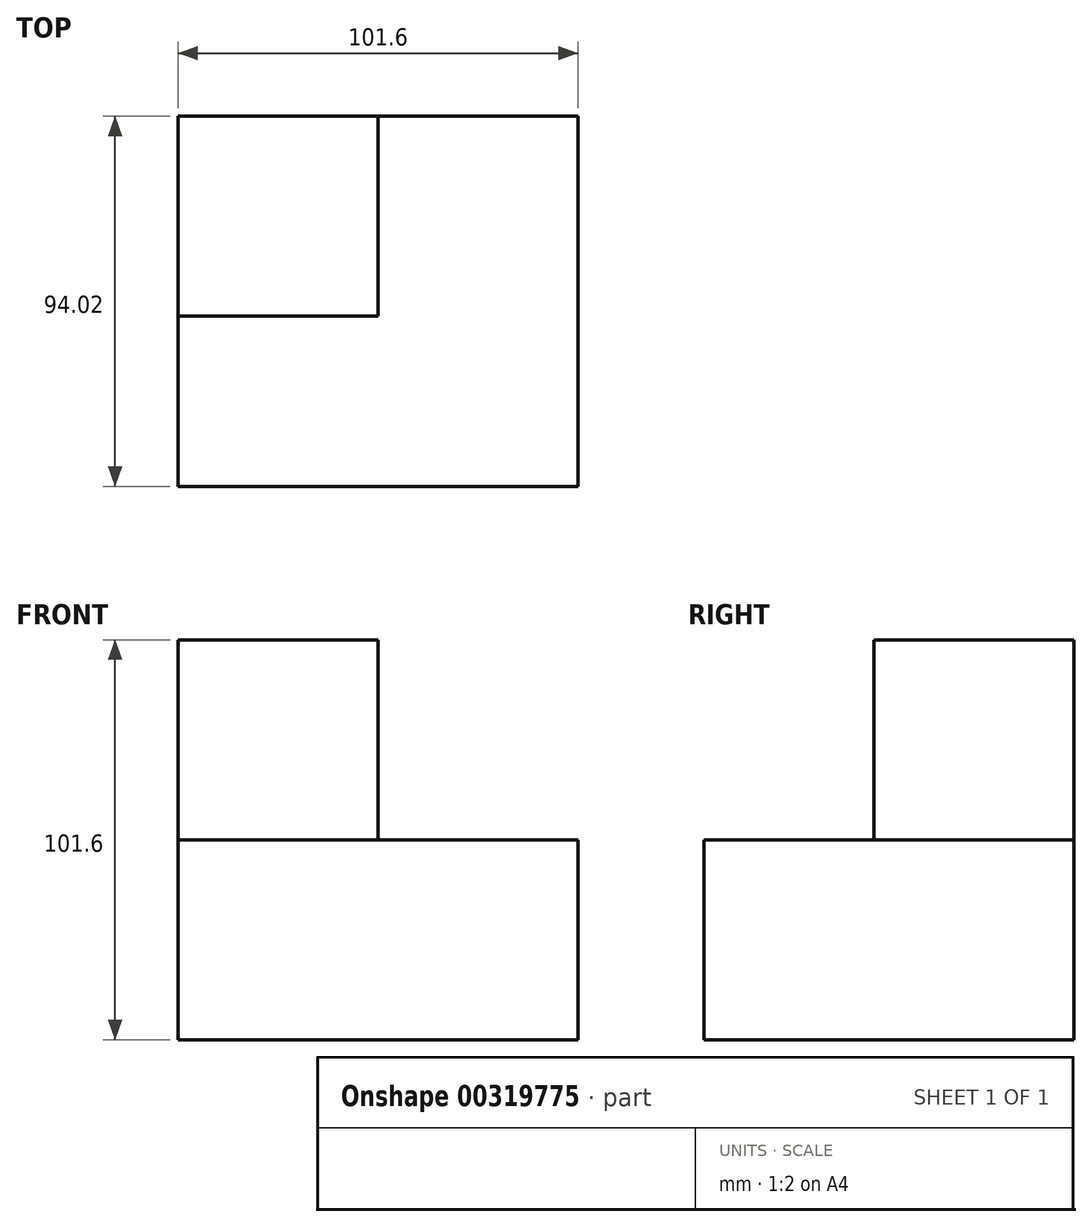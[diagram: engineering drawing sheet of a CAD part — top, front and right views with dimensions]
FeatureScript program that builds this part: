
annotation { "Feature Type Name" : "Feature", "Feature Type Description" : "" }
export const myFeature = defineFeature(function(context is Context, id is Id, definition is map)
    precondition{}
    {
        {
            var Q0;
            Q0=qCreatedBy(makeId("Top.planeOp"),FACE);
            var sketch = newSketch(context, id + "F0", { "sketchPlane" : qUnion([Q0])});
            skLineSegment(sketch, "E0.bottom", {"start": v(-50.8, 47.01) * mm, "end": v(50.8, 47.01) * mm});
            skLineSegment(sketch, "E0.top", {"start": v(-50.8, -47.01) * mm, "end": v(50.8, -47.01) * mm});
            skLineSegment(sketch, "E0.left", {"start": v(-50.8, 47.01) * mm, "end": v(-50.8, -47.01) * mm});
            skLineSegment(sketch, "E0.right", {"start": v(50.8, 47.01) * mm, "end": v(50.8, -47.01) * mm});
            skPoint(sketch, "E0.middle", {"position": v(0, 0) * mm});
            skSolve(sketch);
        }
        {
            var Q0;
            Q0=makeQuery(id+"F0.imprint","IMPRINT",FACE,{"disambiguationData":[TD([[makeQuery(id+"F0.imprint","IMPRINT",EDGE,{"derivedFrom":sQuery(id+"F0.wireOp",EDGE,"E0.bottom")}),-1.0]])]});
            extrude(context, id + "F1", {"entities" : qUnion([Q0]), "depth" : 50.8 * mm});
        }
        {
            var Q0;
            Q0=makeQuery(id+"F1.opExtrude","SWEPT_FACE",FACE,{"disambiguationData":[OSD([sQuery(id+"F0.wireOp",EDGE,"E0.bottom")])]});
            var sketch = newSketch(context, id + "F2", { "sketchPlane" : qUnion([Q0])});
            skLineSegment(sketch, "E1", {"start": v(50.8, 50.8) * mm, "end": v(50.8, 101.6) * mm});
            skLineSegment(sketch, "E2", {"start": v(50.8, 101.6) * mm, "end": v(0, 101.6) * mm});
            skPoint(sketch, "E2.endSnap0", {"position": v(0, 50.8) * mm});
            skLineSegment(sketch, "E3", {"start": v(0, 101.6) * mm, "end": v(0, 50.8) * mm});
            skSolve(sketch);
        }
        {
            var Q0;
            Q0 = qSketchRegion(id + "F2", true);
            var Q1;
            {var subQ0=sQuery(id+"F2.wireOp",EDGE,"E1");Q1=makeQuery(id+"F2.imprint","IMPRINT",FACE,{"disambiguationData":[TD([[makeQuery(id+"F2.imprint","IMPRINT",EDGE,{"derivedFrom":subQ0}),1.0]])]});}
            extrude(context, id + "F3", {"entities" : qUnion([Q0, Q1]), "operationType" : NewBodyOperationType.ADD, "oppositeDirection" : true, "depth" : 50.8 * mm});
        }
    });
